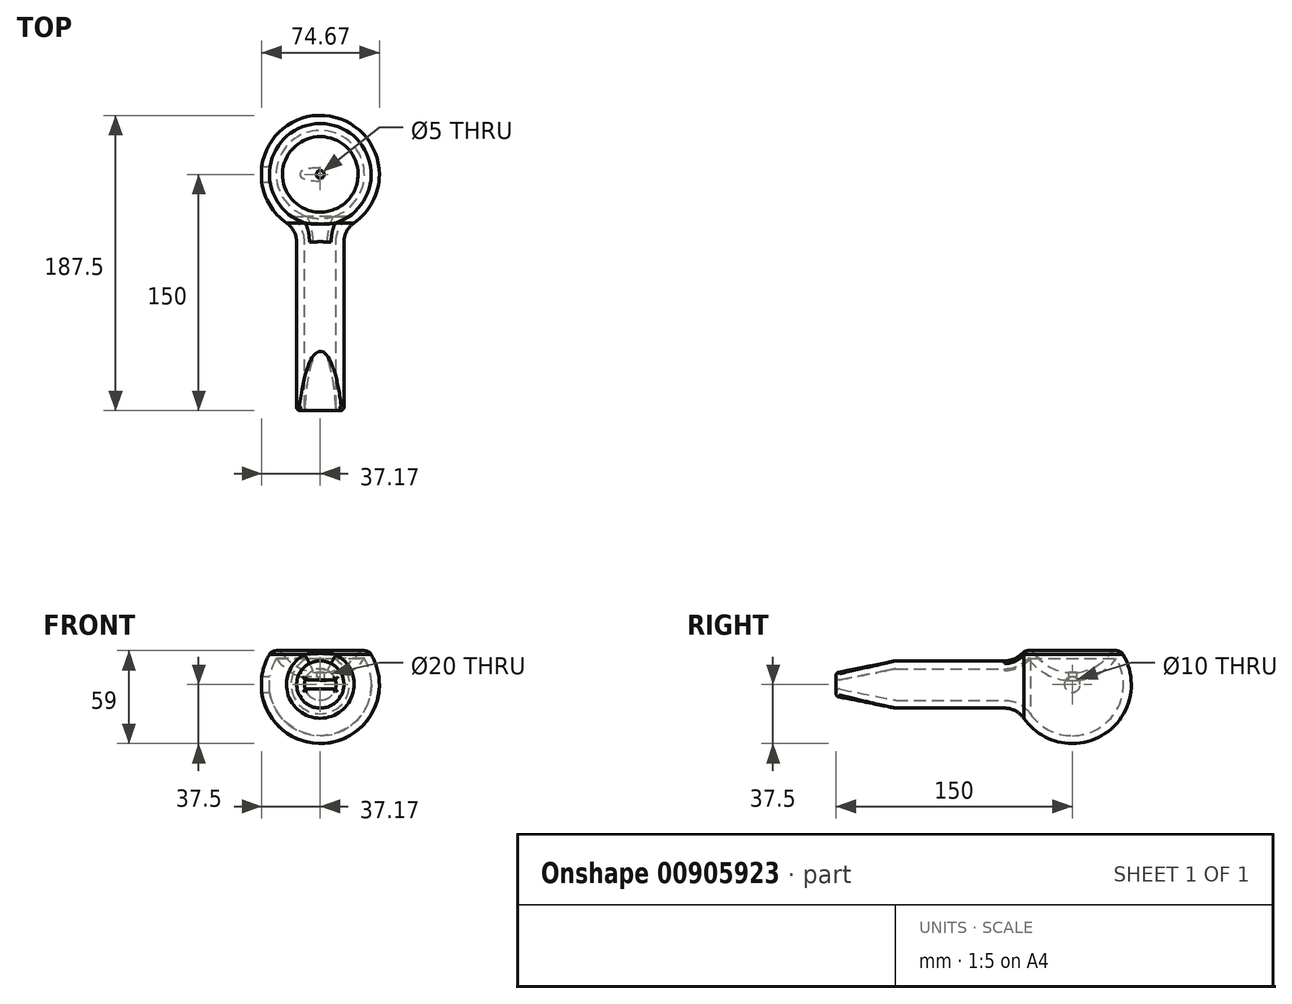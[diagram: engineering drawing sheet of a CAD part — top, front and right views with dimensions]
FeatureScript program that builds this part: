
annotation { "Feature Type Name" : "Feature", "Feature Type Description" : "" }
export const myFeature = defineFeature(function(context is Context, id is Id, definition is map)
    precondition{}
    {
        {
            var Q0;
            Q0=qCreatedBy(makeId("Front.planeOp"),FACE);
            var sketch = newSketch(context, id + "F0", { "sketchPlane" : qUnion([Q0])});
            skLineSegment(sketch, "E0", {"start": v(-37.5, 0) * mm, "end": v(37.5, 0) * mm});
            skArc(sketch, "E1", {"start": v(37.5, 0) * mm, "mid": v(0, 37.5) * mm, "end": v(-37.5, 0) * mm});
            skPoint(sketch, "E2", {"position": v(0, 37.5) * mm});
            skSolve(sketch);
        }
        {
            var Q0;
            Q0 = qSketchRegion(id + "F0", true);
            var Q1;
            Q1=sQuery(id+"F0.wireOp",EDGE,"E0");
            revolve(context, id + "F1", {"surfaceOperationType" : NewSurfaceOperationType.NEW, "entities" : qUnion([Q0]), "axis" : qUnion([Q1]), "revolveType" : RevolveType.FULL});
        }
        {
            var Q0;
            Q0=qCreatedBy(makeId("Front.planeOp"),FACE);
            var sketch = newSketch(context, id + "F2", { "sketchPlane" : qUnion([Q0])});
            skCircle(sketch, "E3", {"center": v(0, 0) * mm, "radius": 15 * mm});
            skSolve(sketch);
        }
        {
            var Q0;
            Q0 = qSketchRegion(id + "F2", true);
            extrude(context, id + "F3", {"entities" : qUnion([Q0]), "operationType" : NewBodyOperationType.ADD, "depth" : 150 * mm, "offsetDistance" : 25 * mm});
        }
        {
            var Q0;
            Q0=qCreatedBy(makeId("Right.planeOp"),FACE);
            var sketch = newSketch(context, id + "F4", { "sketchPlane" : qUnion([Q0])});
            skLineSegment(sketch, "E4", {"start": v(-112.5, 15) * mm, "end": v(-150, 15) * mm});
            skLineSegment(sketch, "E5", {"start": v(-150, 15) * mm, "end": v(-150, 7.5) * mm});
            skLineSegment(sketch, "E6", {"start": v(-150, 7.5) * mm, "end": v(-112.5, 15) * mm});
            skLineSegment(sketch, "E7", {"start": v(-150, -15) * mm, "end": v(-150, 15) * mm, "construction": true});
            skPoint(sketch, "E8", {"position": v(-150, 0) * mm});
            skLineSegment(sketch, "E9", {"start": v(-150, -7.5) * mm, "end": v(-150, -15) * mm});
            skLineSegment(sketch, "E10", {"start": v(-150, -7.5) * mm, "end": v(-112.5, -15) * mm});
            skLineSegment(sketch, "E11", {"start": v(-112.5, -15) * mm, "end": v(-150, -15) * mm});
            skSolve(sketch);
        }
        {
            var Q0;
            Q0 = qSketchRegion(id + "F4", true);
            extrude(context, id + "F5", {"entities" : qUnion([Q0]), "operationType" : NewBodyOperationType.REMOVE, "endBound" : BoundingType.THROUGH_ALL, "oppositeDirection" : true, "depth" : 25 * mm, "offsetDistance" : 25 * mm, "hasSecondDirection" : true, "secondDirectionBound" : SecondDirectionBoundingType.THROUGH_ALL, "secondDirectionOppositeDirection" : false, "secondDirectionDepth" : 25 * mm});
        }
        {
            var Q0;
            Q0=qCreatedBy(makeId("Front.planeOp"),FACE);
            var sketch = newSketch(context, id + "F6", { "sketchPlane" : qUnion([Q0])});
            skLineSegment(sketch, "E12", {"start": v(-30, 37.5) * mm, "end": v(30, 37.5) * mm});
            skArc(sketch, "E13", {"start": v(-30, 37.5) * mm, "mid": v(0, 7.5) * mm, "end": v(30, 37.5) * mm});
            skSolve(sketch);
        }
        {
            var Q0;
            Q0 = qSketchRegion(id + "F6", true);
            var Q1;
            Q1=sQuery(id+"F6.wireOp",EDGE,"E12");
            revolve(context, id + "F7", {"operationType" : NewBodyOperationType.REMOVE, "surfaceOperationType" : NewSurfaceOperationType.NEW, "entities" : qUnion([Q0]), "axis" : qUnion([Q1]), "revolveType" : RevolveType.FULL, "oppositeDirection" : true});
        }
        {
            var Q0;
            Q0=makeQuery(id+"F7.boolean.opBoolean","INTERSECT",EDGE,{"derivedFrom":[makeQuery(id+"F1.opRevolve","SWEPT_FACE",FACE,{"disambiguationData":[OSD([sQuery(id+"F0.wireOp",EDGE,"E1")])]}),makeQuery(id+"F7.opRevolve","SWEPT_FACE",FACE,{"disambiguationData":[OSD([sQuery(id+"F6.wireOp",EDGE,"E13")])]})]});
            fillet(context, id + "F8", {"entities" : qUnion([Q0]), "radius" : 5 * mm, "tangentPropagation" : true, "allowEdgeOverflow" : false});
        }
        {
            var Q0;
            Q0=makeQuery(id+"F3.boolean.opBoolean","INTERSECT",EDGE,{"derivedFrom":[makeQuery(id+"F1.opRevolve","SWEPT_FACE",FACE,{"disambiguationData":[OSD([sQuery(id+"F0.wireOp",EDGE,"E1")])]}),makeQuery(id+"F3.opExtrude","SWEPT_FACE",FACE,{"disambiguationData":[OSD([sQuery(id+"F2.wireOp",EDGE,"E3")])]})]});
            fillet(context, id + "F9", {"entities" : qUnion([Q0]), "radius" : 15 * mm, "tangentPropagation" : true, "allowEdgeOverflow" : false});
        }
        {
            var Q0;
            Q0=makeQuery(id+"F3.opExtrude","CAP_FACE",FACE,{"disambiguationData":[OSD([sQuery(id+"F2.wireOp",EDGE,"E3")])],"isStart":false});
            var Q1;
            Q1=makeQuery(id+"F1.opRevolve","SWEPT_BODY",BODY,{"disambiguationData":[OSD([sQuery(id+"F0.wireOp",EDGE,"E0"),sQuery(id+"F0.wireOp",EDGE,"E1")])]});
            shell(context, id + "F10", {"entities" : qUnion([Q0]), "parts" : qUnion([Q1]), "thickness" : 5 * mm});
        }
        {
            var Q0;
            Q0=qCreatedBy(makeId("Right.planeOp"),FACE);
            var sketch = newSketch(context, id + "F11", { "sketchPlane" : qUnion([Q0])});
            skCircle(sketch, "E14", {"center": v(0, 0) * mm, "radius": 5 * mm});
            skSolve(sketch);
        }
        {
            var Q0;
            Q0 = qSketchRegion(id + "F11", true);
            extrude(context, id + "F12", {"entities" : qUnion([Q0]), "operationType" : NewBodyOperationType.REMOVE, "endBound" : BoundingType.THROUGH_ALL, "oppositeDirection" : true, "depth" : 25 * mm, "offsetDistance" : 25 * mm});
        }
        {
            var Q0;
            Q0=qCreatedBy(makeId("Top.planeOp"),FACE);
            var sketch = newSketch(context, id + "F13", { "sketchPlane" : qUnion([Q0])});
            skCircle(sketch, "E15", {"center": v(0, 0) * mm, "radius": 2.5 * mm});
            skSolve(sketch);
        }
        {
            var Q0;
            Q0 = qSketchRegion(id + "F13", true);
            extrude(context, id + "F14", {"entities" : qUnion([Q0]), "operationType" : NewBodyOperationType.REMOVE, "endBound" : BoundingType.THROUGH_ALL, "depth" : 25 * mm, "offsetDistance" : 25 * mm});
        }
        {
            var Q0;
            Q0=makeQuery(id+"F3.opExtrude","CAP_FACE",FACE,{"disambiguationData":[OSD([sQuery(id+"F2.wireOp",EDGE,"E3")])],"isStart":false});
            var Q1;
            Q1=makeQuery(id+"F5.boolean.opBoolean","COPY",FACE,{"derivedFrom":makeQuery(id+"F5.opExtrude","SWEPT_FACE",FACE,{"disambiguationData":[OSD([sQuery(id+"F4.wireOp",EDGE,"E6")])]})});
            var Q2;
            Q2=makeQuery(id+"F5.boolean.opBoolean","COPY",FACE,{"derivedFrom":makeQuery(id+"F5.opExtrude","SWEPT_FACE",FACE,{"disambiguationData":[OSD([sQuery(id+"F4.wireOp",EDGE,"E10")])]})});
            fillet(context, id + "F15", {"entities" : qUnion([Q0, Q1, Q2]), "radius" : 2 * mm, "tangentPropagation" : true, "allowEdgeOverflow" : false});
        }
    });
